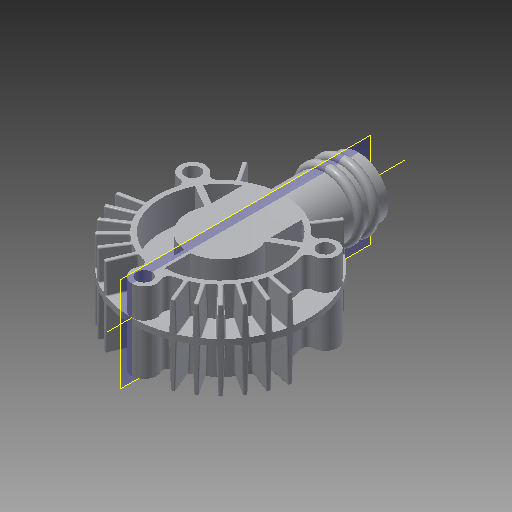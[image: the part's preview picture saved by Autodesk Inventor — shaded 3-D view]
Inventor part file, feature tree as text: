
AUTODESK INVENTOR PART (.ipt)
format: ipt  version: 2017 (Build 210142000, 142)  size: 2,465,280 bytes
history: native  units: in
note: dims shown in document units (in); Inventor stores cm internally (conversion verified against a paired STEP export)
features: sketch x24, extrude x21, pattern_circular x9, plane x4, draft x4, mirror x3, fillet x2, hole x2, revolve x2, other x1, thread x1
ambient origin geometry x8: Origin, YZ Plane, XZ Plane, XY Plane, X Axis, Y Axis, Z Axis, Center Point
bodies: Solid1 (feature_tree)
feature tree (73):
  extrude  "Extrusion1"  Depth=0.05in TaperAngle=0.0deg
  extrude  "Extrusion2"  Depth=1.08in
  extrude  "Extrusion3"  Depth=0.5in
  pattern_circular  "Circular Pattern1"  Count=3 Angle=360.0deg
  plane  "Work Plane2"
  extrude  "Extrusion17"  Depth=0.25in TaperAngle=0.0deg
  extrude  "Extrusion20"  Depth=0.25in
  draft  "FaceDraft5"
  draft  "FaceDraft6"
  fillet  "Fillet6"  Radius=0.125in
  pattern_circular  "Circular Pattern7"  Count=3 Angle=360.0deg
  extrude  "Extrusion21"  Depth=0.25in TaperAngle=360.0deg
  pattern_circular  "Circular Pattern8"  [2 undecoded]
  extrude  "Extrusion22"  Depth=0.25in
  draft  "FaceDraft7"
  draft  "FaceDraft8"
  fillet  "Fillet7"  Radius=0.125in
  pattern_circular  "Circular Pattern9"  [2 undecoded]
  extrude  "Extrusion23"  Depth=0.25in
  pattern_circular  "Circular Pattern10"  [2 undecoded]
  hole  "Hole1"  [1 undecoded]
  pattern_circular  "Circular Pattern11"  [2 undecoded]
  extrude  "Extrusion24"  Depth=0.25in
  plane  "Work Plane5"
  extrude  "Extrusion25"  Depth=0.25in TaperAngle=0.0deg
  hole  "Hole2"  [1 undecoded]
  other  "Work Axis1"
  revolve  "Revolution2"  [1 undecoded]
  pattern_circular  "Circular Pattern2"  [2 undecoded]
  extrude  "Extrusion5"  Depth=0.25in TaperAngle=360.0deg
  extrude  "Extrusion6"  Depth=0.25in
  mirror  "Mirror1"
  mirror  "Mirror2"
  extrude  "Extrusion7"  Depth=0.25in
  extrude  "Extrusion8"  Depth=0.25in TaperAngle=0.0deg
  extrude  "Extrusion9"  Depth=0.25in TaperAngle=360.0deg
  pattern_circular  "Circular Pattern3"  [2 undecoded]
  mirror  "Mirror3"
  extrude  "Extrusion10"  Depth=0.25in
  pattern_circular  "Circular Pattern4"  [2 undecoded]
  extrude  "Extrusion11"  Depth=0.25in
  plane  "Work Plane1"
  extrude  "Extrusion12"  Depth=0.25in TaperAngle=360.0deg
  extrude  "Extrusion13"  Depth=0.25in TaperAngle=0.0deg
  revolve  "Revolution1"  Angle=360.0deg
  extrude  "Extrusion14"  Depth=0.25in
  extrude  "Extrusion16"  Depth=0.25in TaperAngle=360.0deg
  thread  "Thread1"  [1 undecoded]
  sketch  "Sketch1"  dims[d0=1.5in d1=0.05in d2=0.0in]
  sketch  "Sketch2"  dims[d3=1.0in d4=1.08in]
  sketch  "Sketch3"  dims[d5=0.5625in d6=0.5in]
  sketch  "Sketch5"  dims[d7=0.25in d8=0.0in]
  sketch  "Sketch6"  dims[d9=0.05in]
  sketch  "Sketch7"  dims[d10=0.25in d11=0.0in d12=1.1811in d13=360.0deg]
  sketch  "Sketch8"  dims[d20=11.0236in d21=360.0deg d23=0.25in d24=0.0in]
  sketch  "Sketch9"  dims[d25=0.25in d26=0.0in d27=0.5in d28=0.125in d29=0.0in]
  sketch  "Sketch10"  dims[d30=1.0in]
  sketch  "Sketch11"  dims[d31=0.25in d32=0.0in]
  sketch  "Sketch12"  dims[d35=0.25in]
  sketch  "Sketch13"  dims[d36=0.2in]
  sketch  "Sketch14"  dims[d37=0.25in d38=0.0in d39=1.1811in d40=360.0deg]
  sketch  "Sketch15"  dims[d42=0.25in d43=0.0in d44=1.1811in d45=360.0deg]
  sketch  "Sketch17"  dims[d47=0.25in d48=0.0in]
  sketch  "Sketch18"  dims[d49=0.5in]
  sketch  "Sketch20"  dims[d50=0.0625in d51=0.625in d52=0.0in d53=0.0in]
  sketch  "Sketch21"  dims[d54=0.25in d55=0.0in]
  sketch  "Sketch22"  dims[d57=0.1in]
  sketch  "Sketch23"  dims[d58=0.1in]
  sketch  "Sketch24"  dims[d59=0.05in]
  plane  "Work Plane4"
  sketch  "Sketch26"  dims[d60=0.25in]
  sketch  "Sketch27"  dims[d61=0.5in]
  sketch  "Sketch28"  dims[d62=90.0deg d63=0.75in d64=0.0in d67=0.2in d68=0.125in d69=0.0in d70=1.0in d71=0.0in d72=0.25in d76=0.375in d77=0.0in d106=22.5deg d107=0.025in d108=0.025in d109=0.25in d110=0.0in d111=0.0137in d112=0.0137in d113=0.01in d114=12.5984in d115=360.0deg d117=0.1in d118=0.1in d119=0.25in d120=0.0in d121=1.1811in d122=360.0deg d124=0.25in d125=0.0in d126=0.0103in d127=0.0103in d128=0.01in d129=12.5984in d130=360.0deg d132=0.25in d133=0.0in d134=1.1811in d135=360.0deg d137=1.0in d138=1.0in d139=0.129in d140=0.75in d141=0.219in d142=0.112in d143=0.5635in d144=1.0in d145=0.8108in d146=1.1811in d147=360.0deg d149=0.125in d150=0.0in d152=-0.625in d153=0.5in d154=0.5625in d155=0.0in d156=0.313in d157=0.236in d158=0.0246in d159=0.329in d160=0.219in d161=0.112in d162=0.5635in d163=0.25in d164=0.8108in d165=0.125in d166=0.25in d167=90.0deg]
note: 18 required parameter values undecoded (feature->parameter linkage not recoverable at this tier; creation-order binding heuristic only, values carry confidence <= 0.55)